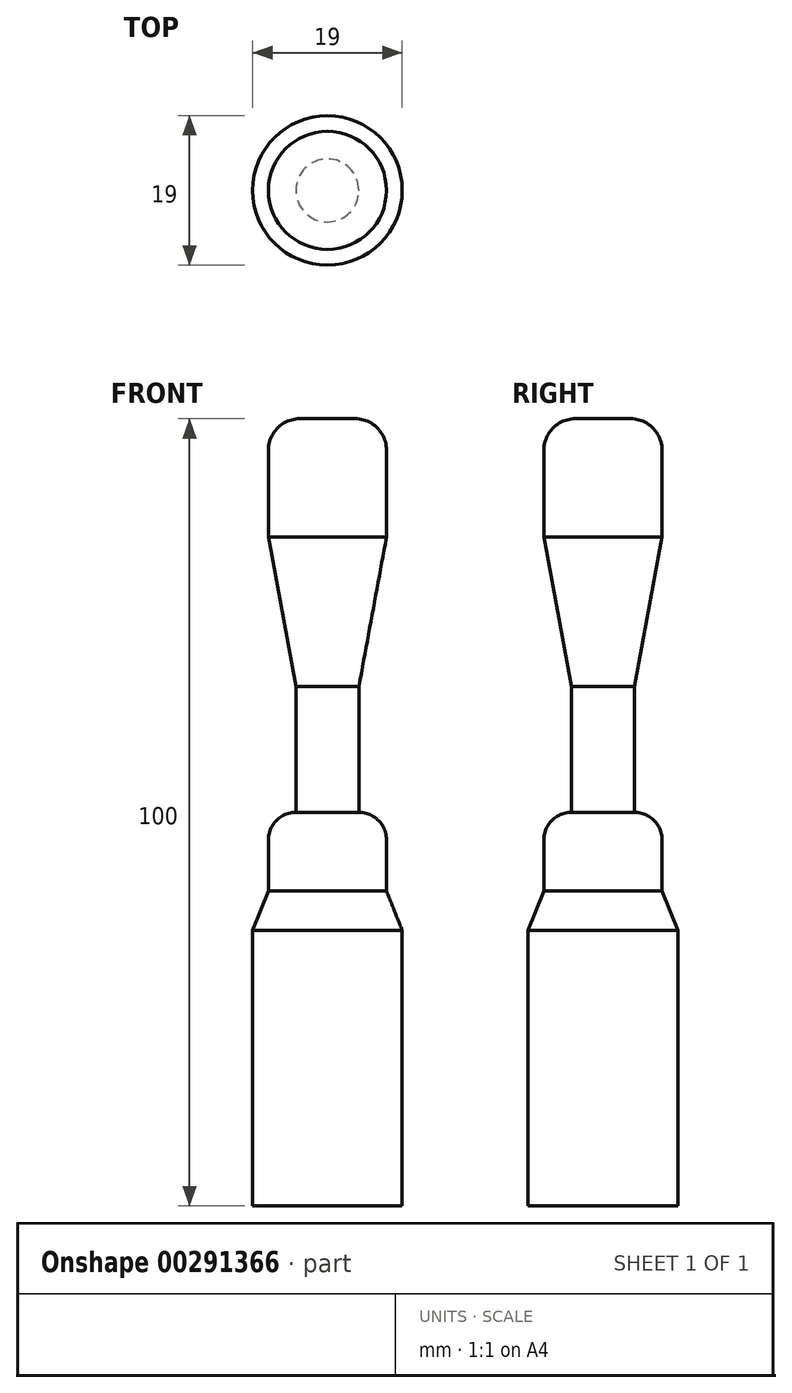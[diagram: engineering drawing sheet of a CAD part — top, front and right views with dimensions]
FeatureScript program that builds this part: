
annotation { "Feature Type Name" : "Feature", "Feature Type Description" : "" }
export const myFeature = defineFeature(function(context is Context, id is Id, definition is map)
    precondition{}
    {
        {
            var Q0;
            Q0=qCreatedBy(makeId("Front.planeOp"),FACE);
            var sketch = newSketch(context, id + "F0", { "sketchPlane" : qUnion([Q0])});
            skLineSegment(sketch, "E0", {"start": v(0, 0) * mm, "end": v(0, -100) * mm});
            skLineSegment(sketch, "E1", {"start": v(0, 0) * mm, "end": v(3.5, 0) * mm});
            skArc(sketch, "E2", {"start": v(7.5, -4) * mm, "mid": v(6.33, -1.17) * mm, "end": v(3.5, 0) * mm});
            skLineSegment(sketch, "E3", {"start": v(7.5, -4) * mm, "end": v(7.5, -15) * mm});
            skLineSegment(sketch, "E4", {"start": v(7.5, -15) * mm, "end": v(4, -34) * mm});
            skLineSegment(sketch, "E5", {"start": v(4, -34) * mm, "end": v(4, -50) * mm});
            skArc(sketch, "E6", {"start": v(7.5, -53.5) * mm, "mid": v(6.47, -51.03) * mm, "end": v(4, -50) * mm});
            skLineSegment(sketch, "E7", {"start": v(7.5, -53.5) * mm, "end": v(7.5, -60) * mm});
            skLineSegment(sketch, "E8", {"start": v(7.5, -60) * mm, "end": v(9.5, -65) * mm});
            skLineSegment(sketch, "E9", {"start": v(9.5, -65) * mm, "end": v(9.5, -100) * mm});
            skLineSegment(sketch, "E10", {"start": v(9.5, -100) * mm, "end": v(0, -100) * mm});
            skSolve(sketch);
        }
        {
            var Q0;
            Q0 = qSketchRegion(id + "F0", true);
            var Q1;
            Q1=sQuery(id+"F0.wireOp",EDGE,"E0");
            revolve(context, id + "F1", {"entities" : qUnion([Q0]), "axis" : qUnion([Q1]), "revolveType" : RevolveType.FULL});
        }
    });
